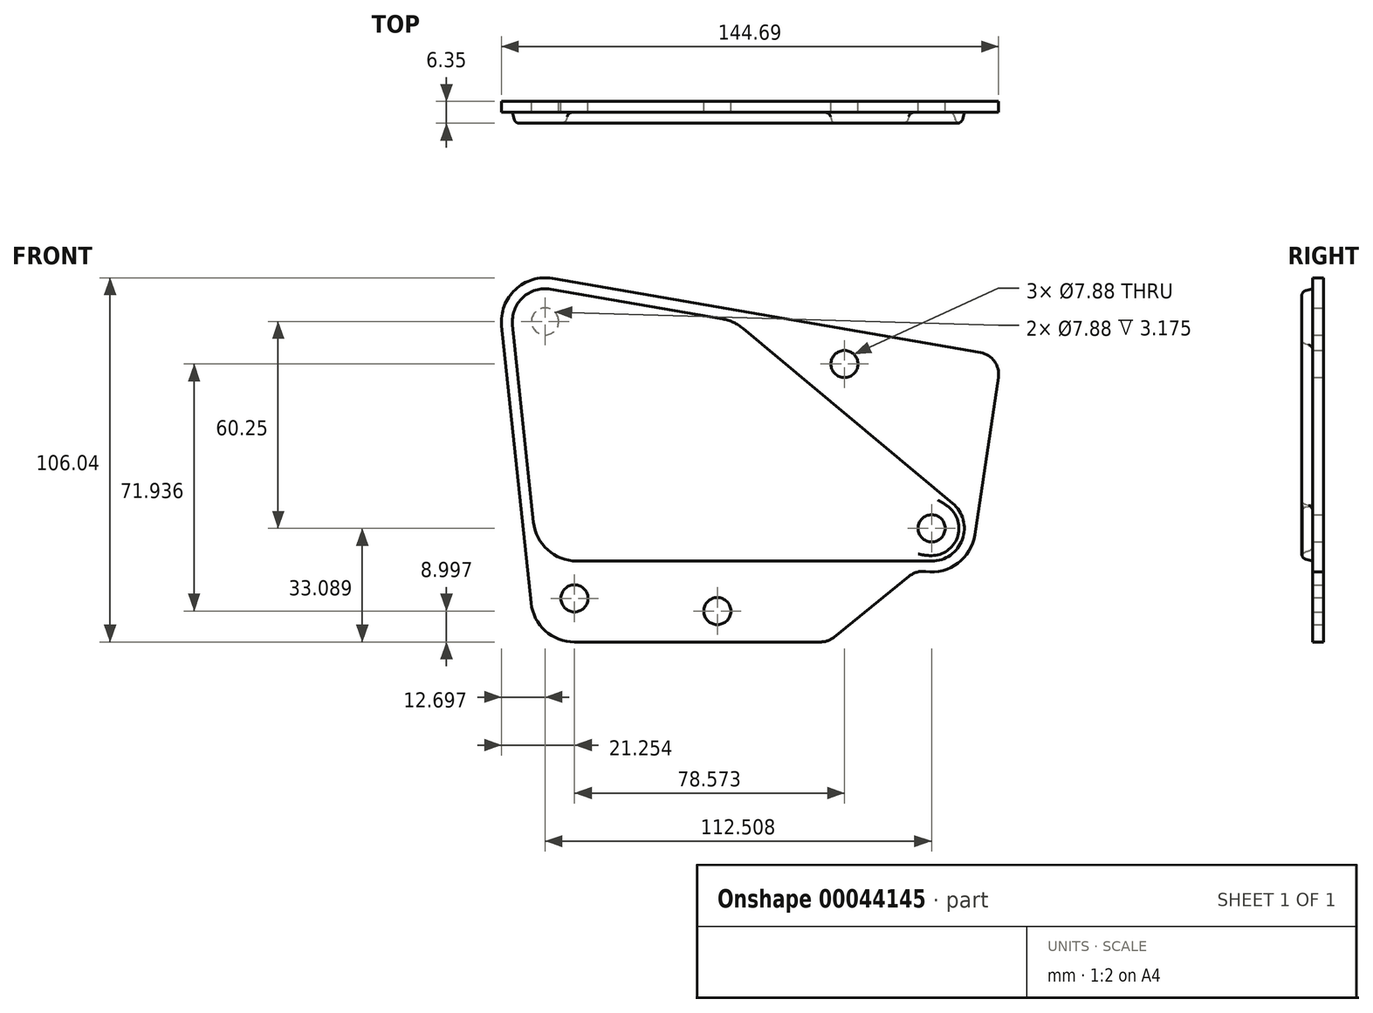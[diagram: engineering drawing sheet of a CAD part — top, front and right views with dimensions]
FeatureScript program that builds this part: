
annotation { "Feature Type Name" : "Feature", "Feature Type Description" : "" }
export const myFeature = defineFeature(function(context is Context, id is Id, definition is map)
    precondition{}
    {
        {
            var Q0;
            Q0=qCreatedBy(makeId("Front.planeOp"),FACE);
            var sketch = newSketch(context, id + "F0", { "sketchPlane" : qUnion([Q0])});
            skLineSegment(sketch, "E0.bottom", {"start": v(-65.7, 39.61) * mm, "end": v(58.87, 18) * mm});
            skLineSegment(sketch, "E0.left", {"start": v(-80.5, 25.76) * mm, "end": v(-71.94, -54.88) * mm});
            skLineSegment(sketch, "E0.right", {"start": v(64.06, 10.81) * mm, "end": v(57.2, -35.03) * mm});
            skPoint(sketch, "E1.visualSharp", {"position": v(64.98, 16.95) * mm});
            skArc(sketch, "E1.filletArc", {"start": v(64.06, 10.81) * mm, "mid": v(62.93, 15.47) * mm, "end": v(58.87, 18) * mm});
            skPoint(sketch, "E2.newPointA", {"position": v(54.23, -54.92) * mm});
            skPoint(sketch, "E2.newPointB", {"position": v(-5593.31, -54.92) * mm});
            skLineSegment(sketch, "E3", {"start": v(38.1, -47.1) * mm, "end": v(16.28, -64.82) * mm});
            skLineSegment(sketch, "E4", {"start": v(12.28, -66.24) * mm, "end": v(-59.3, -66.24) * mm});
            skPoint(sketch, "E5.visualSharp", {"position": v(-70.73, -66.24) * mm});
            skArc(sketch, "E5.filletArc", {"start": v(-71.94, -54.88) * mm, "mid": v(-67.8, -62.98) * mm, "end": v(-59.3, -66.24) * mm});
            skCircle(sketch, "E6", {"center": v(44.64, -33.15) * mm, "radius": 3.94 * mm});
            skCircle(sketch, "E7", {"center": v(-17.72, -57.24) * mm, "radius": 3.94 * mm});
            skCircle(sketch, "E8", {"center": v(-59.3, -53.54) * mm, "radius": 3.94 * mm});
            skCircle(sketch, "E9", {"center": v(19.27, 14.7) * mm, "radius": 3.94 * mm});
            skCircle(sketch, "E10", {"center": v(-67.86, 27.1) * mm, "radius": 3.94 * mm});
            skArc(sketch, "E11", {"start": v(57.2, -35.03) * mm, "mid": v(52.27, -43.3) * mm, "end": v(42.95, -45.74) * mm});
            skArc(sketch, "E12", {"start": v(42.95, -45.74) * mm, "mid": v(40.38, -45.92) * mm, "end": v(38.1, -47.1) * mm});
            skPoint(sketch, "E13.visualSharp", {"position": v(-82.27, 42.49) * mm});
            skArc(sketch, "E13.filletArc", {"start": v(-65.7, 39.61) * mm, "mid": v(-76.54, 36.37) * mm, "end": v(-80.5, 25.76) * mm});
            skPoint(sketch, "E14.visualSharp", {"position": v(14.53, -66.24) * mm});
            skArc(sketch, "E14.filletArc", {"start": v(12.28, -66.24) * mm, "mid": v(14.4, -65.88) * mm, "end": v(16.28, -64.82) * mm});
            skSolve(sketch);
        }
        {
            var Q0;
            Q0=makeQuery(id+"F0.imprint","IMPRINT",FACE,{"disambiguationData":[TD([[makeQuery(id+"F0.imprint","IMPRINT",EDGE,{"derivedFrom":sQuery(id+"F0.wireOp",EDGE,"E0.bottom")}),-1.0]])]});
            extrude(context, id + "F1", {"entities" : qUnion([Q0]), "depth" : 3.17 * mm});
        }
        {
            var Q0;
            Q0=makeQuery(id+"F1.opExtrude","CAP_FACE",FACE,{"disambiguationData":[OSD([sQuery(id+"F0.wireOp",EDGE,"E0.bottom"),sQuery(id+"F0.wireOp",EDGE,"E0.left"),sQuery(id+"F0.wireOp",EDGE,"E0.right"),sQuery(id+"F0.wireOp",EDGE,"E1.filletArc"),sQuery(id+"F0.wireOp",EDGE,"E3"),sQuery(id+"F0.wireOp",EDGE,"E4"),sQuery(id+"F0.wireOp",EDGE,"E5.filletArc"),sQuery(id+"F0.wireOp",EDGE,"E6"),sQuery(id+"F0.wireOp",EDGE,"E7"),sQuery(id+"F0.wireOp",EDGE,"E8"),sQuery(id+"F0.wireOp",EDGE,"E9"),sQuery(id+"F0.wireOp",EDGE,"E10"),sQuery(id+"F0.wireOp",EDGE,"E11"),sQuery(id+"F0.wireOp",EDGE,"E12"),sQuery(id+"F0.wireOp",EDGE,"E13.filletArc"),sQuery(id+"F0.wireOp",EDGE,"E14.filletArc")])],"isStart":false});
            var sketch = newSketch(context, id + "F2", { "sketchPlane" : qUnion([Q0])});
            skLineSegment(sketch, "E15.0", {"start": v(-77.33, 26.1) * mm, "end": v(-71.24, -31.32) * mm});
            skArc(sketch, "E15.1", {"start": v(-66.23, 36.48) * mm, "mid": v(-74.37, 34.05) * mm, "end": v(-77.33, 26.1) * mm});
            skLineSegment(sketch, "E15.2", {"start": v(-66.23, 36.48) * mm, "end": v(-16.2, 27.8) * mm});
            skArc(sketch, "E16", {"start": v(44.64, -42.68) * mm, "mid": v(53.6, -36.4) * mm, "end": v(50.75, -25.84) * mm});
            skLineSegment(sketch, "E17", {"start": v(-10.23, 25.04) * mm, "end": v(50.75, -25.84) * mm});
            skLineSegment(sketch, "E18", {"start": v(-58.61, -42.68) * mm, "end": v(44.64, -42.68) * mm});
            skPoint(sketch, "E19.visualSharp", {"position": v(-70.04, -42.68) * mm});
            skArc(sketch, "E19.filletArc", {"start": v(-71.24, -31.32) * mm, "mid": v(-67.1, -39.42) * mm, "end": v(-58.61, -42.68) * mm});
            skPoint(sketch, "E20.visualSharp", {"position": v(-12.85, 27.22) * mm});
            skArc(sketch, "E20.filletArc", {"start": v(-10.23, 25.04) * mm, "mid": v(-13.04, 26.82) * mm, "end": v(-16.2, 27.8) * mm});
            skLineSegment(sketch, "E21.0", {"start": v(-37.94, -26.4) * mm, "end": v(8.52, -26.4) * mm});
            skLineSegment(sketch, "E21.1", {"start": v(-23.08, 14.58) * mm, "end": v(12.58, -15.18) * mm});
            skArc(sketch, "E22", {"start": v(-23.08, 14.58) * mm, "mid": v(-59.74, 4.68) * mm, "end": v(-37.94, -26.4) * mm});
            skPoint(sketch, "E23.visualSharp", {"position": v(26.04, -26.4) * mm});
            skArc(sketch, "E23.filletArc", {"start": v(8.52, -26.4) * mm, "mid": v(14.49, -22.22) * mm, "end": v(12.58, -15.18) * mm});
            skCircle(sketch, "E24", {"center": v(44.64, -33.15) * mm, "radius": 6.35 * mm});
            skSolve(sketch);
        }
        {
            var Q0;
            Q0 = qSketchRegion(id + "F2", true);
            extrude(context, id + "F3", {"entities" : qUnion([Q0]), "operationType" : NewBodyOperationType.ADD, "depth" : 3.17 * mm, "hasDraft" : true, "draftAngle" : 15 * degree, "draftPullDirection" : true});
        }
        {
            var Q0;
            Q0=makeQuery(id+"F3.opExtrude","CAP_EDGE",EDGE,{"disambiguationData":[OSD([sQuery(id+"F2.wireOp",EDGE,"E18")])],"isStart":true});
            var Q1;
            Q1=makeQuery(id+"F3.opExtrude","CAP_EDGE",EDGE,{"disambiguationData":[OSD([sQuery(id+"F2.wireOp",EDGE,"E18")])],"isStart":false});
            var Q2;
            Q2=makeQuery(id+"F3.opExtrude","CAP_EDGE",EDGE,{"disambiguationData":[OSD([sQuery(id+"F2.wireOp",EDGE,"E24")])],"isStart":false});
            var Q3;
            Q3=makeQuery(id+"F3.opExtrude","CAP_EDGE",EDGE,{"disambiguationData":[OSD([sQuery(id+"F2.wireOp",EDGE,"E24")])],"isStart":true});
            var Q4;
            Q4=makeQuery(id+"F3.opExtrude","CAP_EDGE",EDGE,{"disambiguationData":[OSD([sQuery(id+"F2.wireOp",EDGE,"E21.1")])],"isStart":true});
            var Q5;
            Q5=makeQuery(id+"F3.opExtrude","CAP_EDGE",EDGE,{"disambiguationData":[OSD([sQuery(id+"F2.wireOp",EDGE,"E21.1")])],"isStart":false});
            fillet(context, id + "F4", {"entities" : qUnion([Q0, Q1, Q2, Q3, Q4, Q5]), "radius" : 1.59 * mm, "tangentPropagation" : true, "allowEdgeOverflow" : false});
        }
    });
